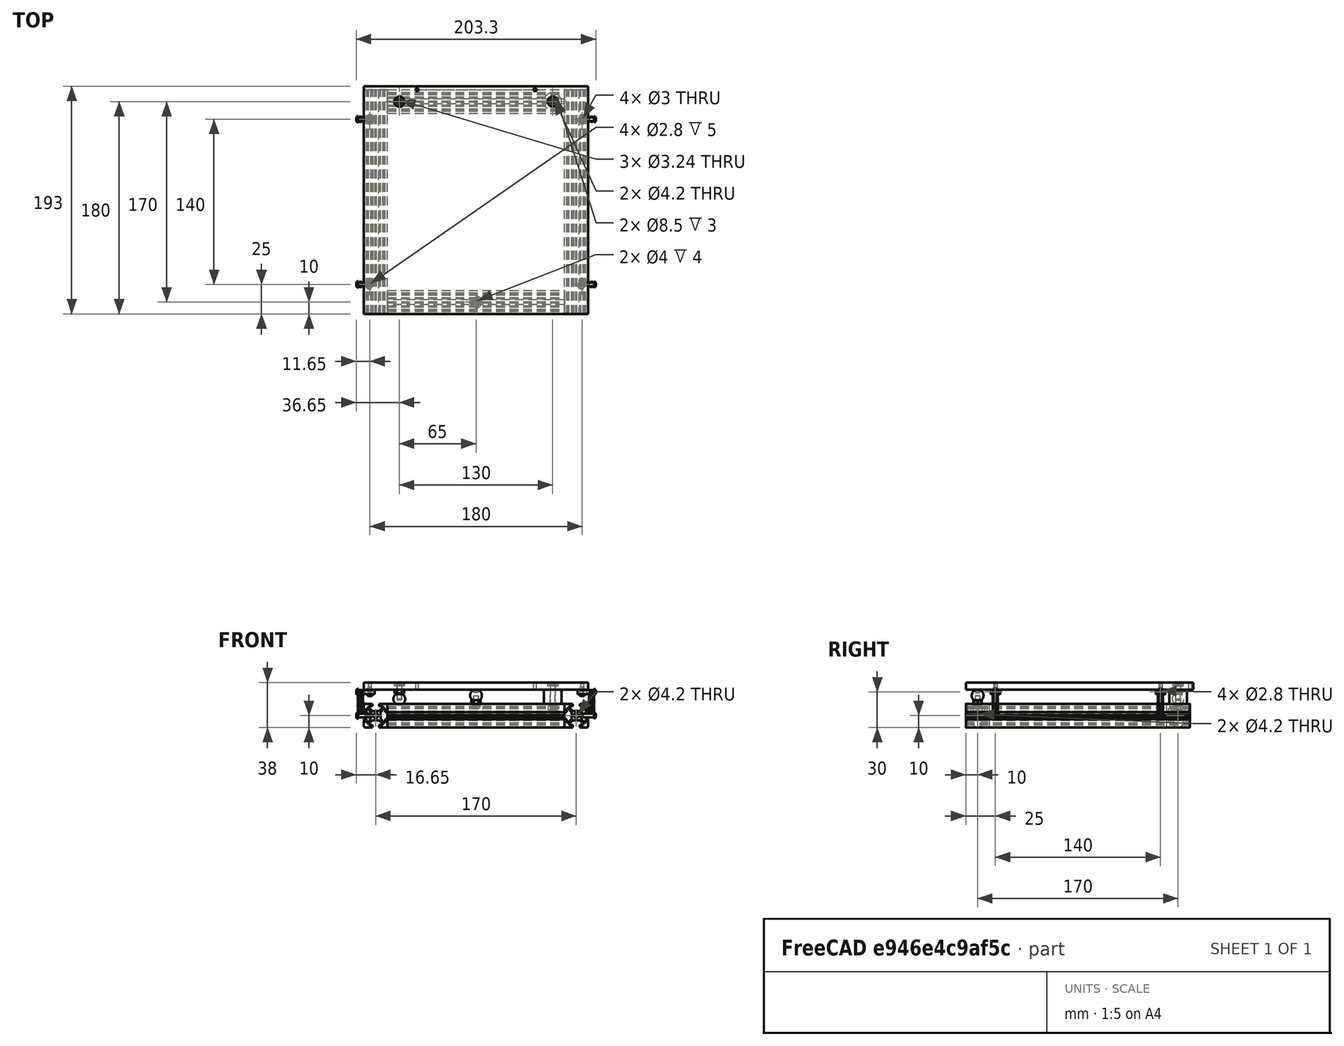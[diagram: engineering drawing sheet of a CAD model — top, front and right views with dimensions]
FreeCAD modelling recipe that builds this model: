
FCSTD DOCUMENT  (FreeCAD 0.19R24291 (Git))
Label: thermal-expansion-compesation-bed-mount-concept
License: All rights reserved
LicenseURL: http://en.wikipedia.org/wiki/All_rights_reserved
objects: Part::FeaturePython×18, Part::Feature×16, App::Part×5
note: 34 computed .brp shape members not serialized (recipe doc carries the construction recipe); baked Part::Feature solids carry a one-line shape summary decoded from their .brp

FEATURE [Part::Feature] Extrude003001  label="2020-190mm001"
  Placement = pos=(-85,-95,2.1e-14) rot=(-1,0,0;1.5708rad)
  shape: bbox 20 x 190 x 20 mm, 63 faces (baked)
FEATURE [Part::Feature] Extrude003003  label="2020-150mm002"
  Placement = pos=(-75,85,-1.7e-14) rot=(0,1,0;1.5708rad)
  shape: bbox 150 x 20 x 20 mm, 63 faces (baked)
FEATURE [Part::Feature] Extrude003002  label="2020-190mm002"
  Placement = pos=(85,-95,2.1e-14) rot=(-1,0,0;1.5708rad)
  shape: bbox 20 x 190 x 20 mm, 63 faces (baked)
FEATURE [Part::Feature] Extrude002002004010  label="2020-150mm001"
  Placement = pos=(-75,-85,-1.7e-14) rot=(0,1,0;1.5708rad)
  shape: bbox 150 x 20 x 20 mm, 63 faces (baked)
FEATURE [App::Part] Part005  label="bed-frame"
  Group = -> [Extrude003001,Extrude002002004010,Extrude003002,Extrude003003]
  Origin = -> Origin005
FEATURE [Part::Feature] Body001001  label="aluminum-plate"
  Placement = pos=(0,0,22) rot=(0,0,1;0rad)
  shape: bbox 190 x 193 x 6 mm, 22 faces (baked)
FEATURE [Part::Feature] Cut001001  label="threaded-ball"
  Placement = pos=(-2e-16,-85,17) rot=(0,1,0;3.14159rad)
  shape: bbox 10 x 10 x 9 mm, 4 faces (baked)
FEATURE [Part::Feature] Cut001002  label="threaded-ball001"
  Placement = pos=(-65,85,14) rot=(0,0,1;0rad)
  shape: bbox 10 x 10 x 9 mm, 4 faces (baked)
FEATURE [Part::Feature] Chamfer001  label="m3-collar"
  Placement = pos=(90,-70,18) rot=(0,0,1;0rad)
  shape: bbox 8 x 8 x 4 mm, 9 faces (baked)
FEATURE [Part::Feature] Chamfer002  label="m3-collar001"
  Placement = pos=(90,70,18) rot=(0,0,1;0rad)
  shape: bbox 8 x 8 x 4 mm, 9 faces (baked)
FEATURE [Part::Feature] Chamfer003  label="m3-collar002"
  Placement = pos=(-90,70,18) rot=(0,0,1;3.14159rad)
  shape: bbox 8 x 8 x 4 mm, 9 faces (baked)
FEATURE [Part::Feature] Chamfer004  label="m3-collar003"
  Placement = pos=(-90,-70,18) rot=(0,0,1;3.14159rad)
  shape: bbox 8 x 8 x 4 mm, 9 faces (baked)
FEATURE [Part::FeaturePython] Screw  label="M4x12-Screw"  # Fasteners workbench fastener (typed FeaturePython)
  Placement = pos=(-65,85,25) rot=(0,0,1;0rad)
  baseObject = -> Body001001 [Edge24]
  diameter = 2
  invert = true
  length = 3
  lengthCustom = 12
  matchOuter = true
  offset = 0
  thread = false
  type = 40
FEATURE [Part::FeaturePython] Nut  label="M4-Nut"  # Fasteners workbench fastener (typed FeaturePython)
  Placement = pos=(-65,85,22) rot=(-1,0,0;3.14159rad)
  baseObject = -> Body001001 [Edge14]
  diameter = 6
  invert = false
  matchOuter = true
  offset = 0
  thread = false
  type = 7
FEATURE [Part::FeaturePython] Screw001  label="M4x20-Screw"  # Fasteners workbench fastener (typed FeaturePython)
  Placement = pos=(65,85,25) rot=(0,0,1;0rad)
  baseObject = -> Body001001 [Edge22]
  diameter = 2
  invert = true
  length = 6
  lengthCustom = 20
  matchOuter = true
  offset = 0
  thread = false
  type = 40
FEATURE [Part::FeaturePython] Nut001  label="M4-Nut001"  # Fasteners workbench fastener (typed FeaturePython)
  Placement = pos=(65,85,8) rot=(-1,0,0;3.14159rad)
  baseObject = -> Body001001 [Edge13]
  diameter = 6
  invert = false
  matchOuter = true
  offset = 14
  thread = false
  type = 7
FEATURE [Part::FeaturePython] Screw002  label="M4x12-Screw001"  # Fasteners workbench fastener (typed FeaturePython)
  Placement = pos=(9e-16,-85,8) rot=(-1,0,0;3.14159rad)
  baseObject = -> Cut001001 [Edge4]
  diameter = 2
  invert = false
  length = 3
  lengthCustom = 12
  matchOuter = true
  offset = 5
  thread = false
  type = 40
FEATURE [Part::FeaturePython] Nut002  label="M4-Nut002"  # Fasteners workbench fastener (typed FeaturePython)
  Placement = pos=(2e-16,-85,13) rot=(-1,0,0;3.14159rad)
  baseObject = -> Cut001001 [Edge4]
  diameter = 6
  invert = false
  matchOuter = true
  offset = 0
  thread = false
  type = 7
FEATURE [App::Part] Part  label="corner-slider"
  Group = -> [Screw,Nut,Cut001002]
  Origin = -> Origin
FEATURE [App::Part] Part006  label="corner-free"
  Group = -> [Screw002,Nut002,Cut001001]
  Origin = -> Origin006
FEATURE [Part::Feature] Tube001001  label="silicon-spacer001"
  Placement = pos=(65,85,10) rot=(0,0,1;0rad)
  shape: bbox 15 x 15 x 12 mm, 4 faces (baked)
FEATURE [App::Part] Part007  label="corner-fixed"
  Group = -> [Nut001,Screw001,Tube001001]
  Origin = -> Origin007
FEATURE [Part::FeaturePython] Screw003  label="M3x6-Screw"  # Fasteners workbench fastener (typed FeaturePython)
  Placement = pos=(-90,-70,18.2) rot=(-1,0,0;3.14159rad)
  baseObject = -> Chamfer004 [Edge18]
  diameter = 1
  invert = true
  length = 0
  lengthCustom = 6
  matchOuter = true
  offset = 0
  thread = false
  type = 40
FEATURE [Part::FeaturePython] Screw004  label="M3x6-Screw004"  # Fasteners workbench fastener (typed FeaturePython)
  Placement = pos=(90,-70,18.2) rot=(-1,0,0;3.14159rad)
  baseObject = -> Chamfer001 [Edge18]
  diameter = 1
  invert = true
  length = 0
  lengthCustom = 6
  matchOuter = true
  offset = 0
  thread = false
  type = 40
FEATURE [Part::FeaturePython] Screw005  label="M3x6-Screw005"  # Fasteners workbench fastener (typed FeaturePython)
  Placement = pos=(90,70,18.2) rot=(-1,0,0;3.14159rad)
  baseObject = -> Chamfer002 [Edge18]
  diameter = 1
  invert = true
  length = 0
  lengthCustom = 6
  matchOuter = true
  offset = 0
  thread = false
  type = 40
FEATURE [Part::FeaturePython] Screw006  label="M3x6-Screw006"  # Fasteners workbench fastener (typed FeaturePython)
  Placement = pos=(-90,70,18.2) rot=(-1,0,0;3.14159rad)
  baseObject = -> Chamfer003 [Edge18]
  diameter = 1
  invert = true
  length = 0
  lengthCustom = 6
  matchOuter = true
  offset = 0
  thread = false
  type = 40
FEATURE [Part::FeaturePython] Screw007  label="M3x10-Screw"  # Fasteners workbench fastener (typed FeaturePython)
  Placement = pos=(-100,-70,20) rot=(0,1,0;4.71239rad)
  diameter = 1
  invert = false
  length = 2
  lengthCustom = 10
  matchOuter = true
  offset = 0
  thread = false
  type = 40
FEATURE [Part::FeaturePython] Screw008  label="M3x10-Screw001"  # Fasteners workbench fastener (typed FeaturePython)
  Placement = pos=(-100,70,20) rot=(0,-1,0;1.5708rad)
  diameter = 1
  invert = false
  length = 2
  lengthCustom = 10
  matchOuter = true
  offset = 0
  thread = false
  type = 40
FEATURE [Part::FeaturePython] Screw009  label="M3x10-Screw002"  # Fasteners workbench fastener (typed FeaturePython)
  Placement = pos=(100,70,20) rot=(0.707107,0,0.707107;3.14159rad)
  diameter = 1
  invert = false
  length = 2
  lengthCustom = 10
  matchOuter = true
  offset = 0
  thread = false
  type = 40
FEATURE [Part::FeaturePython] Screw010  label="M3x10-Screw003"  # Fasteners workbench fastener (typed FeaturePython)
  Placement = pos=(100,-70,20) rot=(0.707107,0,0.707107;3.14159rad)
  diameter = 1
  invert = false
  length = 2
  lengthCustom = 10
  matchOuter = true
  offset = 0
  thread = false
  type = 40
FEATURE [Part::FeaturePython] Screw011  label="M3x10-Screw008"  # Fasteners workbench fastener (typed FeaturePython)
  Placement = pos=(-100,-70,-2.13e-14) rot=(0,-1,0;1.5708rad)
  diameter = 1
  invert = false
  length = 2
  lengthCustom = 10
  matchOuter = true
  offset = 0
  thread = false
  type = 40
FEATURE [Part::FeaturePython] Screw012  label="M3x10-Screw009"  # Fasteners workbench fastener (typed FeaturePython)
  Placement = pos=(-100,70,-2.13e-14) rot=(0,-1,0;1.5708rad)
  diameter = 1
  invert = false
  length = 2
  lengthCustom = 10
  matchOuter = true
  offset = 0
  thread = false
  type = 40
FEATURE [Part::FeaturePython] Screw013  label="M3x10-Screw010"  # Fasteners workbench fastener (typed FeaturePython)
  Placement = pos=(100,70,-6.75e-14) rot=(0.707107,0,0.707107;3.14159rad)
  diameter = 1
  invert = false
  length = 2
  lengthCustom = 10
  matchOuter = true
  offset = 0
  thread = false
  type = 40
FEATURE [Part::FeaturePython] Screw014  label="M3x10-Screw011"  # Fasteners workbench fastener (typed FeaturePython)
  Placement = pos=(100,-70,-6.75e-14) rot=(0.707107,0,0.707107;3.14159rad)
  diameter = 1
  invert = false
  length = 2
  lengthCustom = 10
  matchOuter = true
  offset = 0
  thread = false
  type = 40
FEATURE [Part::Feature] Body001001001001001  label="hook-spring-001"
  Placement = pos=(-121,-54,-14) rot=(0,0,1;0rad)
  shape: bbox 4.558 x 4.635 x 20.91 mm, 22 faces (baked)
FEATURE [Part::Feature] Body001001001001002  label="hook-spring-002"
  Placement = pos=(-121,86,-14) rot=(0,0,1;0rad)
  shape: bbox 4.558 x 4.635 x 20.91 mm, 22 faces (baked)
FEATURE [Part::Feature] Body001001001001003  label="hook-spring-003"
  Placement = pos=(75,-54,-14) rot=(0,0,1;0rad)
  shape: bbox 4.558 x 4.635 x 20.91 mm, 22 faces (baked)
FEATURE [Part::Feature] Body001001001001004  label="hook-spring-004"
  Placement = pos=(75,86,-14) rot=(0,0,1;0rad)
  shape: bbox 4.558 x 4.635 x 20.91 mm, 22 faces (baked)
FEATURE [App::Part] Part008  label="collars"
  Group = -> [Chamfer001,Chamfer002,Chamfer003,Chamfer004,Screw006,Screw005,Screw004,Screw003,Screw007,Screw008,Screw009,Screw010,Screw011,Screw012,Screw013,Screw014,Body001001001001001,Body001001001001002,Body001001001001003,Body001001001001004]
  Origin = -> Origin008
